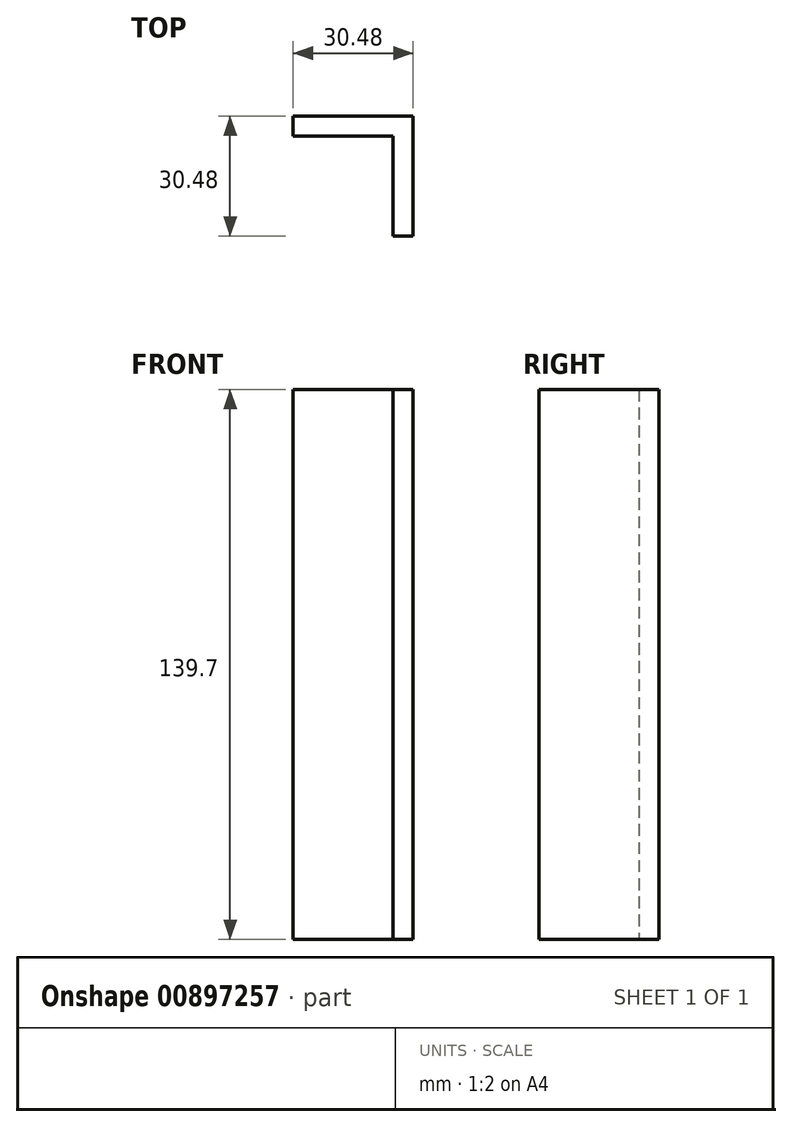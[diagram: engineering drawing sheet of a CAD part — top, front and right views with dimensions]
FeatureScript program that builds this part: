
annotation { "Feature Type Name" : "Feature", "Feature Type Description" : "" }
export const myFeature = defineFeature(function(context is Context, id is Id, definition is map)
    precondition{}
    {
        {
            var Q0;
            Q0=qCreatedBy(makeId("Top.planeOp"),FACE);
            var sketch = newSketch(context, id + "F0", { "sketchPlane" : qUnion([Q0])});
            skLineSegment(sketch, "E0.bottom", {"start": v(0, 0) * mm, "end": v(-5.08, 0) * mm});
            skLineSegment(sketch, "E0.top", {"start": v(0, -25.4) * mm, "end": v(-5.08, -25.4) * mm});
            skLineSegment(sketch, "E0.left", {"start": v(0, 0) * mm, "end": v(0, -25.4) * mm});
            skLineSegment(sketch, "E0.right", {"start": v(-5.08, 0) * mm, "end": v(-5.08, -25.4) * mm});
            skLineSegment(sketch, "E1.bottom", {"start": v(0, 0) * mm, "end": v(-30.48, 0) * mm});
            skLineSegment(sketch, "E1.top", {"start": v(0, 5.08) * mm, "end": v(-30.48, 5.08) * mm});
            skLineSegment(sketch, "E1.left", {"start": v(0, 0) * mm, "end": v(0, 5.08) * mm});
            skLineSegment(sketch, "E1.right", {"start": v(-30.48, 0) * mm, "end": v(-30.48, 5.08) * mm});
            skSolve(sketch);
        }
        {
            var Q0;
            Q0=makeQuery(id+"F0.imprint","IMPRINT",FACE,{"disambiguationData":[TD([[makeQuery(id+"F0.imprint","IMPRINT",EDGE,{"derivedFrom":sQuery(id+"F0.wireOp",EDGE,"E0.top")}),-1.0]])]});
            var Q1;
            Q1=makeQuery(id+"F0.imprint","IMPRINT",FACE,{"disambiguationData":[TD([[makeQuery(id+"F0.imprint","IMPRINT",EDGE,{"derivedFrom":sQuery(id+"F0.wireOp",EDGE,"E1.top")}),1.0]])]});
            extrude(context, id + "F1", {"entities" : qUnion([Q0, Q1]), "depth" : 139.7 * mm, "offsetDistance" : 25.4 * mm});
        }
    });
